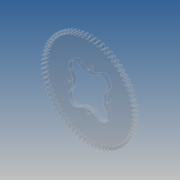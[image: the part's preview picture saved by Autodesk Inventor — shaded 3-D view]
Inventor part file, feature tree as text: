
AUTODESK INVENTOR PART (.ipt)
format: ipt  version: 2017 (Build 210142000, 142)  size: 463,872 bytes
history: native  units: mm
features: other x6, reference x5, extrude x1, sketch x1
ambient origin geometry x8: Origin, YZ Plane, XZ Plane, XY Plane, X Axis, Y Axis, Z Axis, Center Point
bodies: Body1 (feature_tree)
feature tree (13):
  other  "Sólido1"
  extrude  "Extrusión1"  Depth=5.0mm
  other  "Dientes de engranaje recto1"
  sketch  "Boceto1"  dims[d0=30.0mm d1=150.0mm d2=5.0mm d3=0.0mm]
  reference  "Referencia1"
  reference  "Referencia2"
  reference  "Referencia3"
  reference  "Referencia4"
  reference  "Referencia5"
  other  "Engranaje recto2"
  other  "<userpath>\Dropbox\E\Caja Motriz\transmision Engranajes\Plato Carrete.iam"
  other  "Plato Carrete.iam"
  other  "carrete:1"
